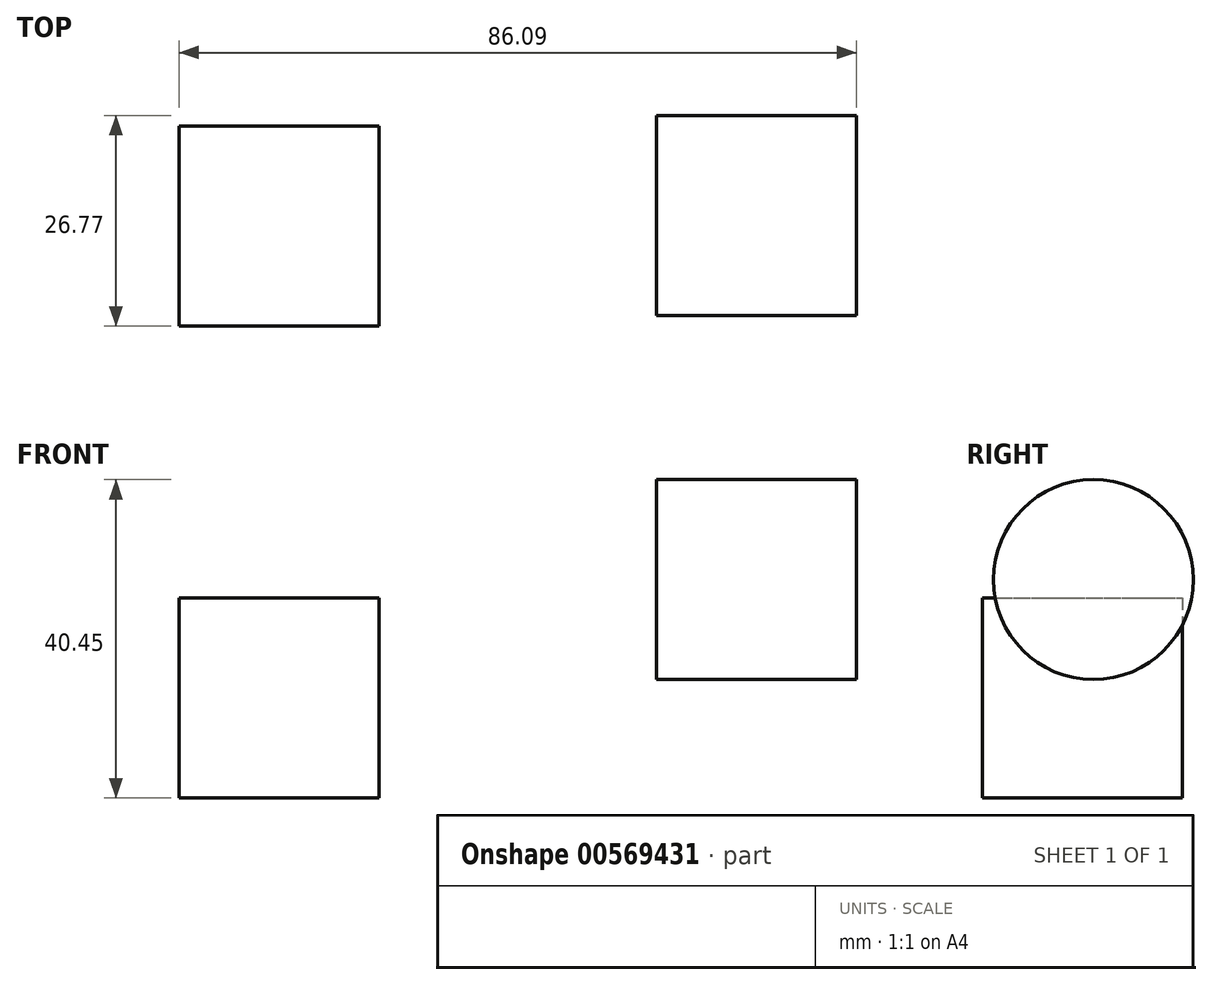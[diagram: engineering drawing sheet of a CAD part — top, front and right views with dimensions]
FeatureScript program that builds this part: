
annotation { "Feature Type Name" : "Feature", "Feature Type Description" : "" }
export const myFeature = defineFeature(function(context is Context, id is Id, definition is map)
    precondition{}
    {
        {
            var Q0;
            Q0=qCreatedBy(makeId("Front.planeOp"),FACE);
            var sketch = newSketch(context, id + "F0", { "sketchPlane" : qUnion([Q0])});
            skLineSegment(sketch, "E0.bottom", {"start": v(-60.69, 55.61) * mm, "end": v(-35.29, 55.61) * mm});
            skLineSegment(sketch, "E0.top", {"start": v(-60.69, 30.21) * mm, "end": v(-35.29, 30.21) * mm});
            skLineSegment(sketch, "E0.left", {"start": v(-60.69, 55.61) * mm, "end": v(-60.69, 30.21) * mm});
            skLineSegment(sketch, "E0.right", {"start": v(-35.29, 55.61) * mm, "end": v(-35.29, 30.21) * mm});
            skSolve(sketch);
        }
        {
            var Q0;
            Q0=makeQuery(id+"F0.imprint","IMPRINT",FACE,{"disambiguationData":[TD([[makeQuery(id+"F0.imprint","IMPRINT",EDGE,{"derivedFrom":sQuery(id+"F0.wireOp",EDGE,"E0.bottom")}),-1.0]])]});
            extrude(context, id + "F1", {"entities" : qUnion([Q0]), "depth" : 25.4 * mm, "offsetDistance" : 25.4 * mm});
        }
        {
            var Q0;
            Q0=qCreatedBy(makeId("Right.planeOp"),FACE);
            var sketch = newSketch(context, id + "F2", { "sketchPlane" : qUnion([Q0])});
            skCircle(sketch, "E1", {"center": v(-11.33, 57.96) * mm, "radius": 12.7 * mm});
            skSolve(sketch);
        }
        {
            var Q0;
            Q0=makeQuery(id+"F2.imprint","IMPRINT",FACE,{"disambiguationData":[TD([[makeQuery(id+"F2.imprint","IMPRINT",EDGE,{"derivedFrom":sQuery(id+"F2.wireOp",EDGE,"E1")}),1.0]])]});
            extrude(context, id + "F3", {"entities" : qUnion([Q0]), "depth" : 25.4 * mm, "offsetDistance" : 25.4 * mm});
        }
    });
